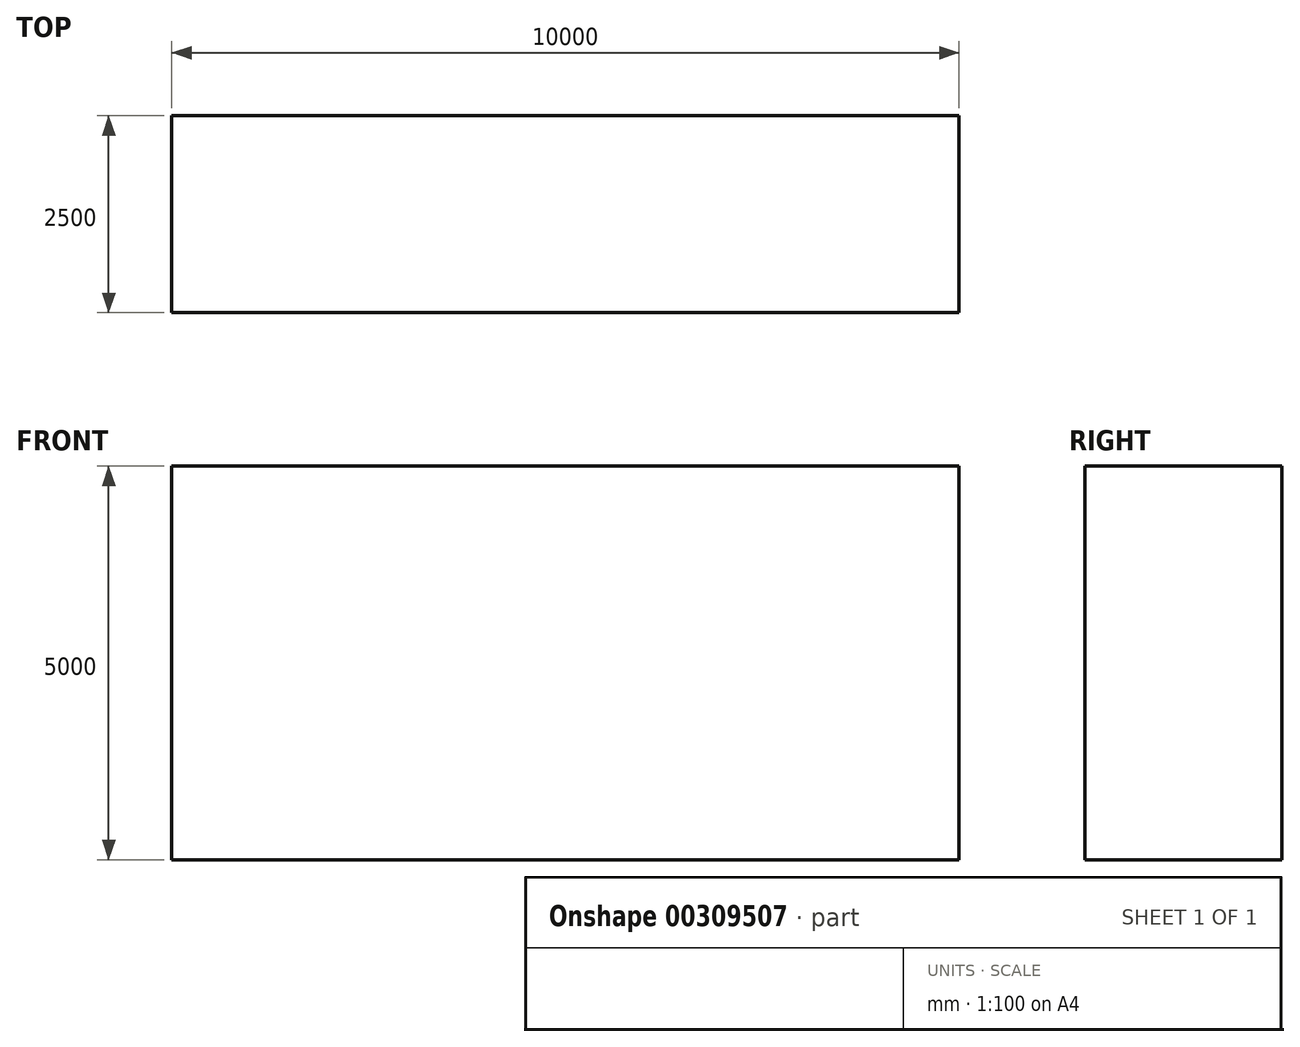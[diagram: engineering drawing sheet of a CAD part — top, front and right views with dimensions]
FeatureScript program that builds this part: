
annotation { "Feature Type Name" : "Feature", "Feature Type Description" : "" }
export const myFeature = defineFeature(function(context is Context, id is Id, definition is map)
    precondition{}
    {
        {
            var Q0;
            Q0=qCreatedBy(makeId("Front.planeOp"),FACE);
            var sketch = newSketch(context, id + "F0", { "sketchPlane" : qUnion([Q0])});
            skLineSegment(sketch, "E0.bottom", {"start": v(-4991.7, 1903.96) * mm, "end": v(5008.3, 1903.96) * mm});
            skLineSegment(sketch, "E0.top", {"start": v(-4991.7, -3096.04) * mm, "end": v(5008.3, -3096.04) * mm});
            skLineSegment(sketch, "E0.left", {"start": v(-4991.7, 1903.96) * mm, "end": v(-4991.7, -3096.04) * mm});
            skLineSegment(sketch, "E0.right", {"start": v(5008.3, 1903.96) * mm, "end": v(5008.3, -3096.04) * mm});
            skSolve(sketch);
        }
        {
            var Q0;
            Q0 = qSketchRegion(id + "F0", true);
            extrude(context, id + "F1", {"entities" : qUnion([Q0]), "depth" : 2500 * mm});
        }
    });
